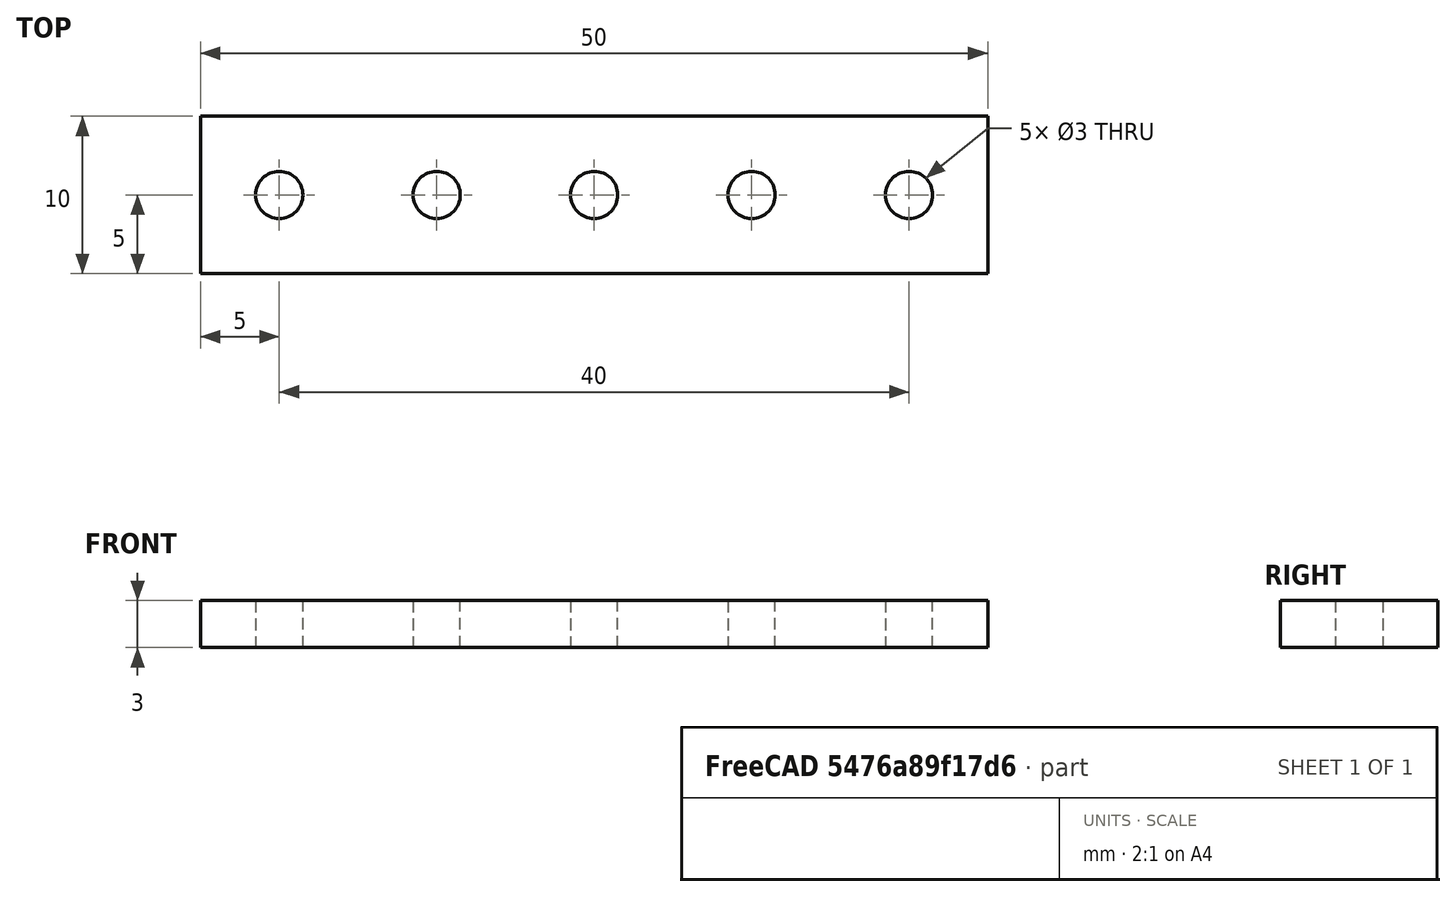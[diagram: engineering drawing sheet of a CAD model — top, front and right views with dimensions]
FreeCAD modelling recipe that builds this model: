
FCSTD DOCUMENT  (FreeCAD 0.20R29177 +233 (Git))
Label: Reto_3_pieza_mecano
License: Creative Commons Attribution-ShareAlike
LicenseURL: http://creativecommons.org/licenses/by-sa/4.0/
objects: Part::Cylinder×5, Part::Cut×5, Part::Box×1
note: 11 computed .brp shape members not serialized (recipe doc carries the construction recipe); baked Part::Feature solids carry a one-line shape summary decoded from their .brp

FEATURE [Part::Box] Box  label="Cubo"
  AttacherType = Attacher::AttachEngine3D
  Height = 3
  Length = 50
  Width = 10
FEATURE [Part::Cylinder] Cylinder  label="Cilindro"
  Angle = 360
  AttacherType = Attacher::AttachEngine3D
  FirstAngle = 0
  Height = 10
  Placement = pos=(5,5,-1) rot=(0,0,1;0rad)
  Radius = 1.5
  SecondAngle = 0
FEATURE [Part::Cut] Cut
  Base = -> Box
  Tool = -> Cylinder
FEATURE [Part::Cylinder] Cylinder001  label="Cilindro001"
  Angle = 360
  AttacherType = Attacher::AttachEngine3D
  FirstAngle = 0
  Height = 10
  Placement = pos=(15,5,-1) rot=(0,0,1;0rad)
  Radius = 1.5
  SecondAngle = 0
FEATURE [Part::Cylinder] Cylinder002  label="Cilindro002"
  Angle = 360
  AttacherType = Attacher::AttachEngine3D
  FirstAngle = 0
  Height = 10
  Placement = pos=(25,5,-1) rot=(0,0,1;0rad)
  Radius = 1.5
  SecondAngle = 0
FEATURE [Part::Cylinder] Cylinder003  label="Cilindro003"
  Angle = 360
  AttacherType = Attacher::AttachEngine3D
  FirstAngle = 0
  Height = 10
  Placement = pos=(35,5,-1) rot=(0,0,1;0rad)
  Radius = 1.5
  SecondAngle = 0
FEATURE [Part::Cylinder] Cylinder004  label="Cilindro004"
  Angle = 360
  AttacherType = Attacher::AttachEngine3D
  FirstAngle = 0
  Height = 10
  Placement = pos=(45,5,-1) rot=(0,0,1;0rad)
  Radius = 1.5
  SecondAngle = 0
FEATURE [Part::Cut] Cut001
  Base = -> Cut
  Tool = -> Cylinder001
FEATURE [Part::Cut] Cut002
  Base = -> Cut001
  Tool = -> Cylinder002
FEATURE [Part::Cut] Cut003
  Base = -> Cut002
  Tool = -> Cylinder003
FEATURE [Part::Cut] Cut004
  Base = -> Cut003
  Tool = -> Cylinder004
